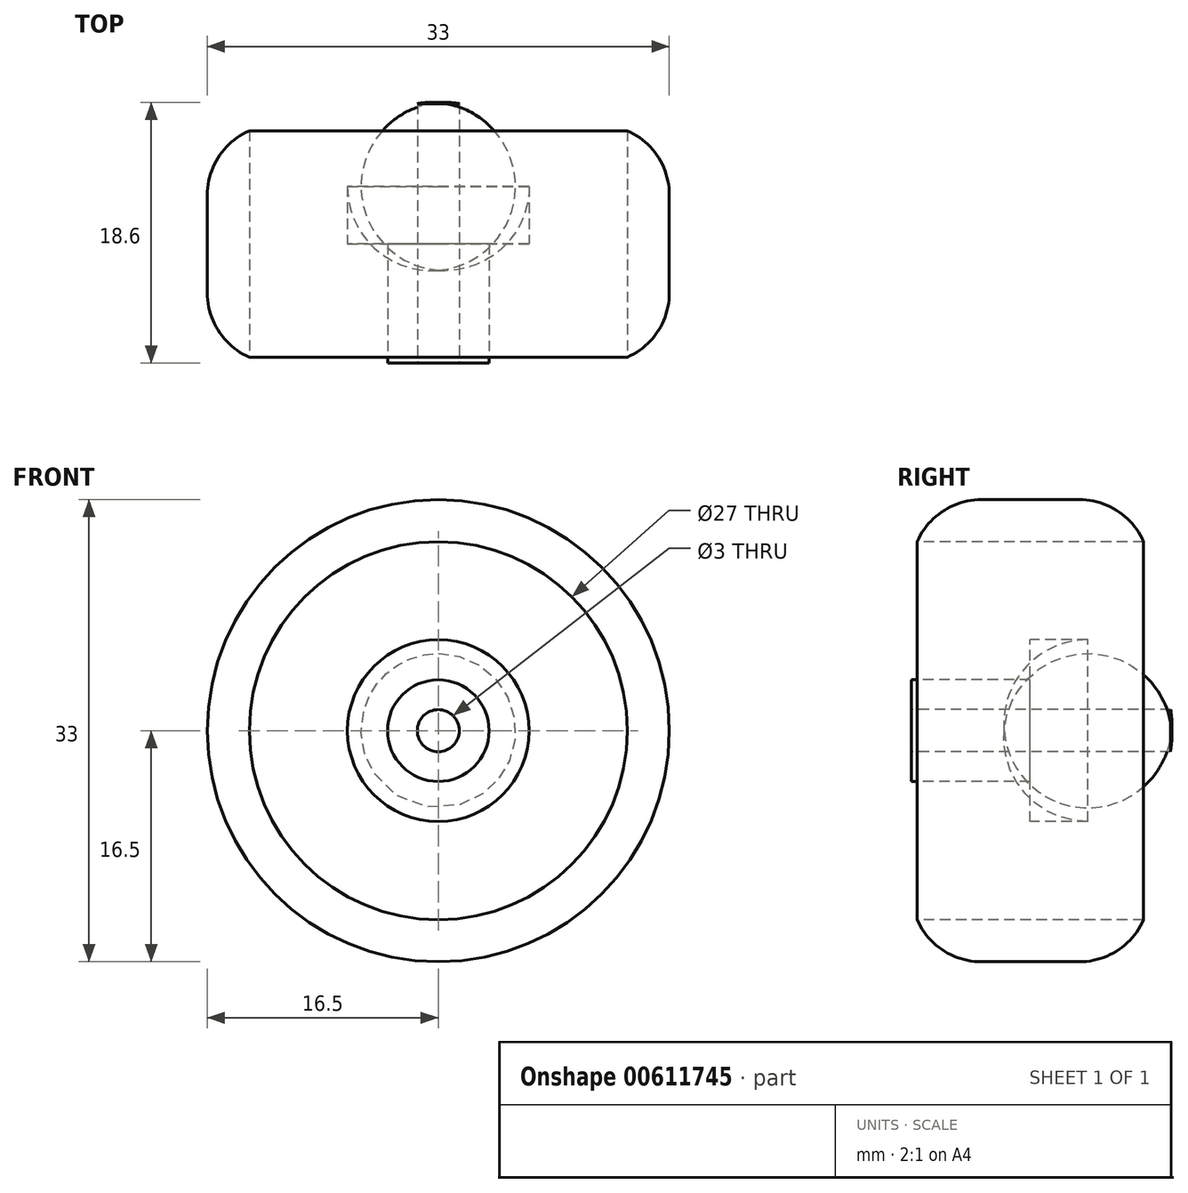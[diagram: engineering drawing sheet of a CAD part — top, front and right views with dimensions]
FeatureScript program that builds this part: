
annotation { "Feature Type Name" : "Feature", "Feature Type Description" : "" }
export const myFeature = defineFeature(function(context is Context, id is Id, definition is map)
    precondition{}
    {
        {
            var Q0;
            Q0=qCreatedBy(makeId("Right.planeOp"),FACE);
            var sketch = newSketch(context, id + "F0", { "sketchPlane" : qUnion([Q0])});
            skLineSegment(sketch, "E0.top", {"start": v(5, 16.5) * mm, "end": v(12, 16.5) * mm});
            skLineSegment(sketch, "E0.left", {"start": v(0, 1.5) * mm, "end": v(0, 11.5) * mm});
            skLineSegment(sketch, "E0.right", {"start": v(17, 11.5) * mm, "end": v(17, 13.5) * mm});
            skLineSegment(sketch, "E1", {"start": v(17, 13.5) * mm, "end": v(0, 13.5) * mm});
            skLineSegment(sketch, "E2", {"start": v(0, 3.63) * mm, "end": v(8.5, 3.63) * mm});
            skLineSegment(sketch, "E3", {"start": v(8.5, 3.63) * mm, "end": v(8.5, 6.5) * mm});
            skLineSegment(sketch, "E4", {"start": v(8.5, 6.5) * mm, "end": v(12.6, 6.5) * mm});
            skLineSegment(sketch, "E5", {"start": v(18.6, 1.5) * mm, "end": v(18.6, 0.5) * mm});
            skLineSegment(sketch, "E6", {"start": v(0, 1.5) * mm, "end": v(18.6, 1.5) * mm});
            skPoint(sketch, "E7.orphan", {"position": v(18.6, 0) * mm});
            skPoint(sketch, "E8.orphan", {"position": v(0, 0) * mm});
            skLineSegment(sketch, "E9", {"start": v(-34.54, 0) * mm, "end": v(39.75, 0) * mm, "construction": true});
            skLineSegment(sketch, "E10", {"start": v(26.2, 9.25) * mm, "end": v(49.6, 4.93) * mm, "construction": true});
            skPoint(sketch, "E11.visualSharp", {"position": v(0, 16.5) * mm});
            skArc(sketch, "E11.filletArc", {"start": v(5, 16.5) * mm, "mid": v(1.46, 15.04) * mm, "end": v(0, 11.5) * mm});
            skPoint(sketch, "E12.visualSharp", {"position": v(17, 16.5) * mm});
            skArc(sketch, "E12.filletArc", {"start": v(17, 11.5) * mm, "mid": v(15.54, 15.04) * mm, "end": v(12, 16.5) * mm});
            skPoint(sketch, "E13.visualSharp", {"position": v(18.6, 6.5) * mm});
            skArc(sketch, "E13.filletArc", {"start": v(18.6, 0.5) * mm, "mid": v(16.85, 4.73) * mm, "end": v(12.6, 6.5) * mm});
            skSolve(sketch);
        }
        {
            var Q0;
            {var subQ0=sQuery(id+"F0.wireOp",EDGE,"E0.top");Q0=makeQuery(id+"F0.imprint","IMPRINT",FACE,{"disambiguationData":[TD([[makeQuery(id+"F0.imprint","IMPRINT",EDGE,{"derivedFrom":subQ0}),-1.0]])]});}
            var Q1;
            {var subQ0=sQuery(id+"F0.wireOp",EDGE,"E2");Q1=makeQuery(id+"F0.imprint","IMPRINT",FACE,{"disambiguationData":[TD([[makeQuery(id+"F0.imprint","IMPRINT",EDGE,{"derivedFrom":subQ0}),-1.0]])]});}
            var Q2;
            Q2=sQuery(id+"F0.wireOp",EDGE,"E9");
            revolve(context, id + "F1", {"entities" : qUnion([Q0, Q1]), "axis" : qUnion([Q2]), "revolveType" : RevolveType.FULL});
        }
    });
